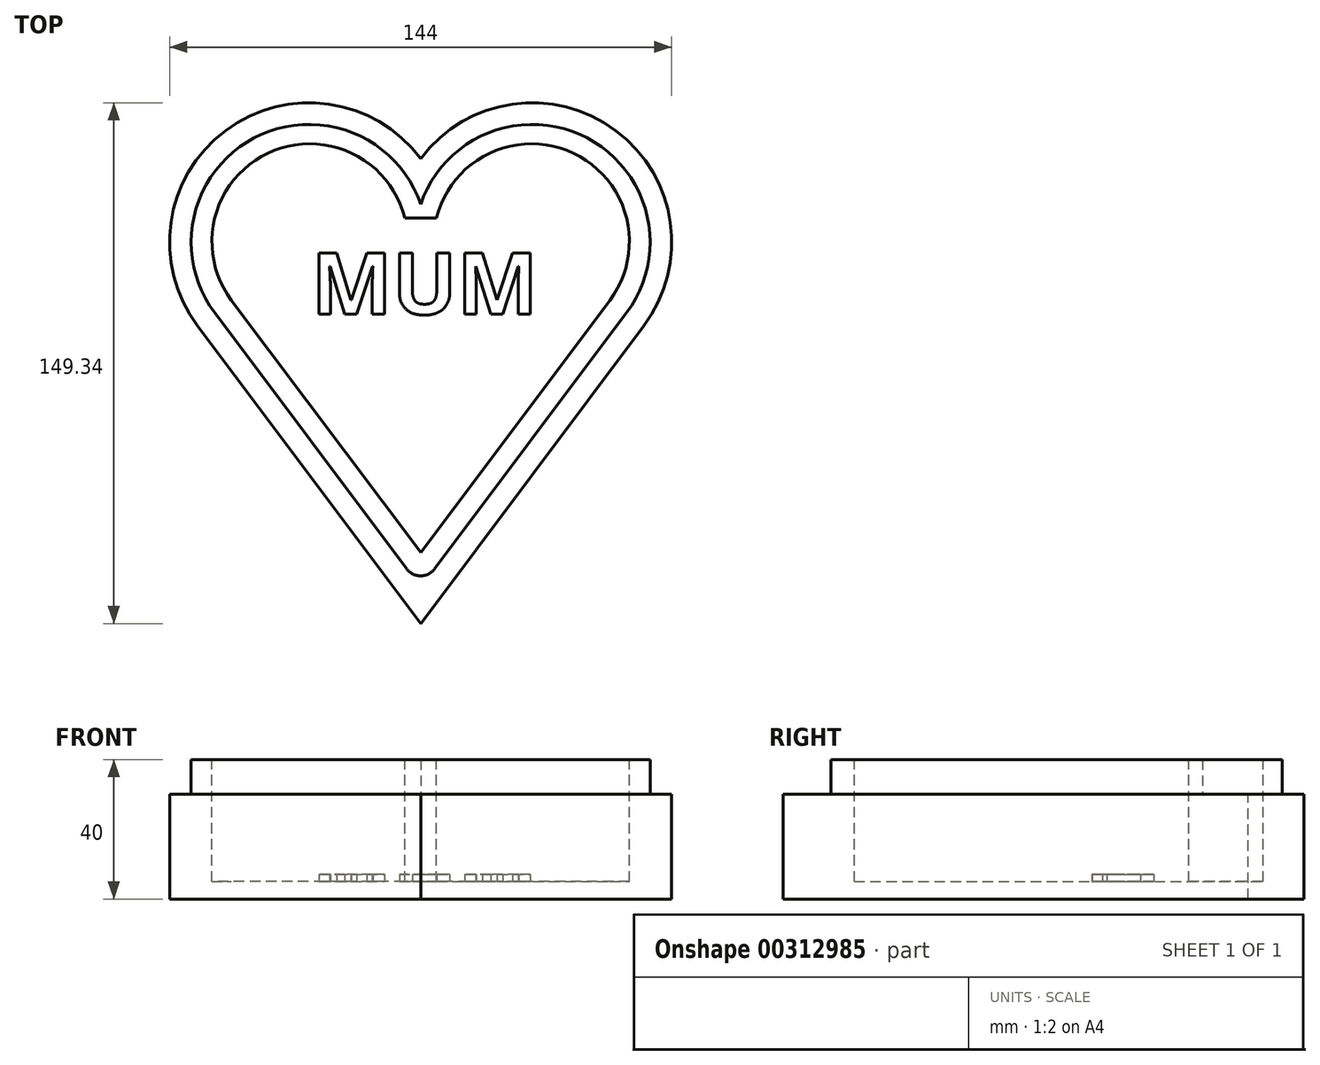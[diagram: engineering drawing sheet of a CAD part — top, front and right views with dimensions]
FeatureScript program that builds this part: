
annotation { "Feature Type Name" : "Feature", "Feature Type Description" : "" }
export const myFeature = defineFeature(function(context is Context, id is Id, definition is map)
    precondition{}
    {
        {
            var Q0;
            Q0=qCreatedBy(makeId("Top.planeOp"),FACE);
            var sketch = newSketch(context, id + "F0", { "sketchPlane" : qUnion([Q0])});
            skLineSegment(sketch, "E0", {"start": v(0, -77.83) * mm, "end": v(-64, 7.5) * mm});
            skArc(sketch, "E1", {"start": v(0, 55.5) * mm, "mid": v(-56, 63.5) * mm, "end": v(-64, 7.5) * mm});
            skArc(sketch, "E2.MirrorCS", {"start": v(0, 55.5) * mm, "mid": v(56, 63.5) * mm, "end": v(64, 7.5) * mm});
            skLineSegment(sketch, "E3.MirrorCS", {"start": v(0, -77.83) * mm, "end": v(64, 7.5) * mm});
            skLineSegment(sketch, "E4.0", {"start": v(0, -67.5) * mm, "end": v(-59.04, 11.23) * mm});
            skLineSegment(sketch, "E4.1", {"start": v(0, -67.5) * mm, "end": v(59.04, 11.23) * mm});
            skArc(sketch, "E4.2", {"start": v(0, 42.39) * mm, "mid": v(47.78, 61.4) * mm, "end": v(59.04, 11.23) * mm});
            skArc(sketch, "E4.3", {"start": v(0, 42.39) * mm, "mid": v(-47.78, 61.4) * mm, "end": v(-59.04, 11.23) * mm});
            skSolve(sketch);
        }
        {
            var Q0;
            Q0=makeQuery(id+"F0.imprint","IMPRINT",FACE,{"disambiguationData":[TD([[makeQuery(id+"F0.imprint","IMPRINT",EDGE,{"derivedFrom":sQuery(id+"F0.wireOp",EDGE,"E4.0")}),-1.0]])]});
            extrude(context, id + "F1", {"entities" : qUnion([Q0]), "depth" : 10 * mm});
        }
        {
            var Q0;
            Q0 = qSketchRegion(id + "F0", true);
            var Q1;
            Q1=makeQuery(id+"F0.imprint","IMPRINT",FACE,{"disambiguationData":[TD([[makeQuery(id+"F0.imprint","IMPRINT",EDGE,{"derivedFrom":sQuery(id+"F0.wireOp",EDGE,"E4.0")}),-1.0]])]});
            extrude(context, id + "F2", {"entities" : qUnion([Q0, Q1]), "operationType" : NewBodyOperationType.ADD, "oppositeDirection" : true, "depth" : 30 * mm});
        }
        {
            var Q0;
            Q0=makeQuery(id+"F1.opExtrude","CAP_FACE",FACE,{"disambiguationData":[OSD([sQuery(id+"F0.wireOp",EDGE,"E4.0"),sQuery(id+"F0.wireOp",EDGE,"E4.1"),sQuery(id+"F0.wireOp",EDGE,"E4.2"),sQuery(id+"F0.wireOp",EDGE,"E4.3")])],"isStart":false});
            var sketch = newSketch(context, id + "F3", { "sketchPlane" : qUnion([Q0])});
            skLineSegment(sketch, "E5", {"start": v(0, -57.5) * mm, "end": v(-54.24, 14.83) * mm});
            skArc(sketch, "E6", {"start": v(-4.56, 38.48) * mm, "mid": v(-43.85, 57.01) * mm, "end": v(-54.24, 14.83) * mm});
            skLineSegment(sketch, "E7", {"start": v(-4.56, 38.48) * mm, "end": v(0, 38.48) * mm});
            skLineSegment(sketch, "E8", {"start": v(0, 66.73) * mm, "end": v(0, -67.5) * mm, "construction": true});
            skLineSegment(sketch, "E9.MirrorCS", {"start": v(4.56, 38.48) * mm, "end": v(0, 38.48) * mm});
            skArc(sketch, "E10.MirrorCS", {"start": v(4.56, 38.48) * mm, "mid": v(43.85, 57.01) * mm, "end": v(54.24, 14.83) * mm});
            skLineSegment(sketch, "E11.MirrorCS", {"start": v(0, -57.5) * mm, "end": v(54.24, 14.83) * mm});
            skSolve(sketch);
        }
        {
            var Q0;
            Q0=makeQuery(id+"F3.imprint","IMPRINT",FACE,{"disambiguationData":[TD([[makeQuery(id+"F3.imprint","IMPRINT",EDGE,{"derivedFrom":sQuery(id+"F3.wireOp",EDGE,"E5")}),-1.0]])]});
            extrude(context, id + "F4", {"entities" : qUnion([Q0]), "operationType" : NewBodyOperationType.REMOVE, "oppositeDirection" : true, "depth" : 35 * mm});
        }
        {
            var Q0;
            Q0=makeQuery(id+"F4.boolean.opBoolean","COPY",FACE,{"derivedFrom":makeQuery(id+"F4.opExtrude","CAP_FACE",FACE,{"disambiguationData":[OSD([sQuery(id+"F3.wireOp",EDGE,"E5"),sQuery(id+"F3.wireOp",EDGE,"E6"),sQuery(id+"F3.wireOp",EDGE,"E7"),sQuery(id+"F3.wireOp",EDGE,"E9.MirrorCS"),sQuery(id+"F3.wireOp",EDGE,"E10.MirrorCS"),sQuery(id+"F3.wireOp",EDGE,"E11.MirrorCS")])],"isStart":false})});
            var sketch = newSketch(context, id + "F5", { "sketchPlane" : qUnion([Q0])});
            skText(sketch, "E12", { "text": "MUM", "fontName": "OpenSans-Bold.ttf"});
            const initialGuessF5  = {"E12": [-0.03142, 0.01083, 1, 0, 0.01774]};
            skSetInitialGuess(sketch, initialGuessF5);
            skSolve(sketch);
        }
        {
            var Q0;
            Q0 = qSketchRegion(id + "F5", true);
            extrude(context, id + "F6", {"entities" : qUnion([Q0]), "operationType" : NewBodyOperationType.ADD, "depth" : 2 * mm});
        }
        {
            var Q0;
            Q0=makeQuery(id+"F1.opExtrude","SWEPT_EDGE",EDGE,{"disambiguationData":[OSD([sQuery(id+"F0.wireOp",EDGE,"E4.0"),sQuery(id+"F0.wireOp",EDGE,"E4.1")])]});
            fillet(context, id + "F7", {"entities" : qUnion([Q0]), "radius" : 5 * mm, "tangentPropagation" : true, "allowEdgeOverflow" : false});
        }
    });
